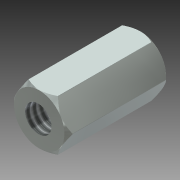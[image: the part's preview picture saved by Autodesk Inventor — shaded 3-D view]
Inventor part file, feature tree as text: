
AUTODESK INVENTOR PART (.ipt)
format: ipt  version: 2013 (Build 170138000, 138)  size: 139,776 bytes
history: native  units: mm (DEFAULTED — no unit token found)
features: sketch x4, plane x2, hole x2, extrude x1, revolve x1
ambient origin geometry x8: Origin, YZ Plane, XZ Plane, XY Plane, X Axis, Y Axis, Z Axis, Center Point
bodies: Solid1 (feature_tree)
feature tree (10):
  extrude  "Extrusion1"  Depth=12.7mm TaperAngle=0.0deg
  plane  "Work Plane1"
  revolve  "Revolution1"  [1 undecoded]
  hole  "Hole3"  [1 undecoded]
  hole  "Hole4"  [1 undecoded]
  plane  "Work Plane2"
  sketch  "Sketch1"  dims[d0=6.35mm d1=12.7mm d2=0.0mm]
  sketch  "Sketch3"  dims[d4=-3.175mm d5=0.508mm]
  sketch  "Sketch6"  dims[d6=0.508mm d7=0.508mm]
  sketch  "Sketch7"  dims[d8=0.508mm d16=0.0mm d17=90.0deg d32=3.302mm d33=12.7mm d34=9.525mm d35=6.35mm d36=14.3117mm d37=6.35mm d38=20.594885mm d39=3.302mm d40=19.05mm d41=9.525mm d42=6.35mm d43=14.3117mm d44=6.35mm d45=20.594885mm d46=0.508mm d47=0.508mm d48=0.508mm d49=0.508mm]
note: 3 required parameter values undecoded (feature->parameter linkage not recoverable at this tier; creation-order binding heuristic only, values carry confidence <= 0.55)